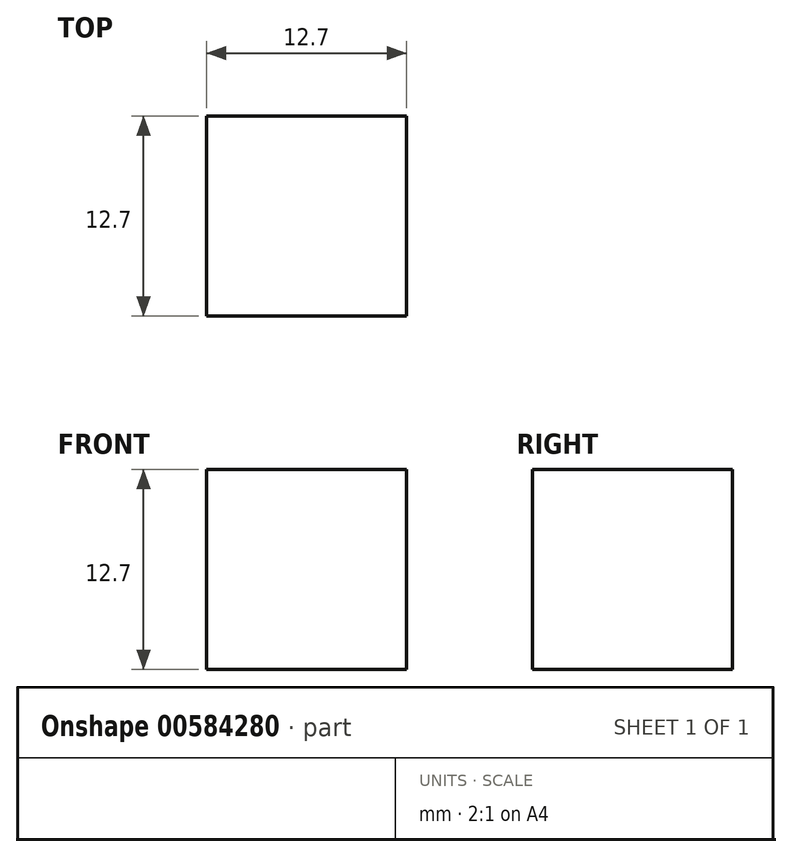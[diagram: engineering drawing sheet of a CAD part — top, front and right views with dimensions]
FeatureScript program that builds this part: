
annotation { "Feature Type Name" : "Feature", "Feature Type Description" : "" }
export const myFeature = defineFeature(function(context is Context, id is Id, definition is map)
    precondition{}
    {
        {
            var Q0;
            Q0=qCreatedBy(makeId("Top.planeOp"),FACE);
            var sketch = newSketch(context, id + "F0", { "sketchPlane" : qUnion([Q0])});
            skLineSegment(sketch, "E0.bottom", {"start": v(0, 0) * mm, "end": v(12.7, 0) * mm});
            skLineSegment(sketch, "E0.top", {"start": v(0, -12.7) * mm, "end": v(12.7, -12.7) * mm});
            skLineSegment(sketch, "E0.left", {"start": v(0, 0) * mm, "end": v(0, -12.7) * mm});
            skLineSegment(sketch, "E0.right", {"start": v(12.7, 0) * mm, "end": v(12.7, -12.7) * mm});
            skSolve(sketch);
        }
        {
            var Q0;
            Q0=makeQuery(id+"F0.imprint","IMPRINT",FACE,{"disambiguationData":[TD([[makeQuery(id+"F0.imprint","IMPRINT",EDGE,{"derivedFrom":sQuery(id+"F0.wireOp",EDGE,"E0.bottom")}),-1.0]])]});
            extrude(context, id + "F1", {"entities" : qUnion([Q0]), "depth" : 12.7 * mm, "offsetDistance" : 25.4 * mm});
        }
    });
